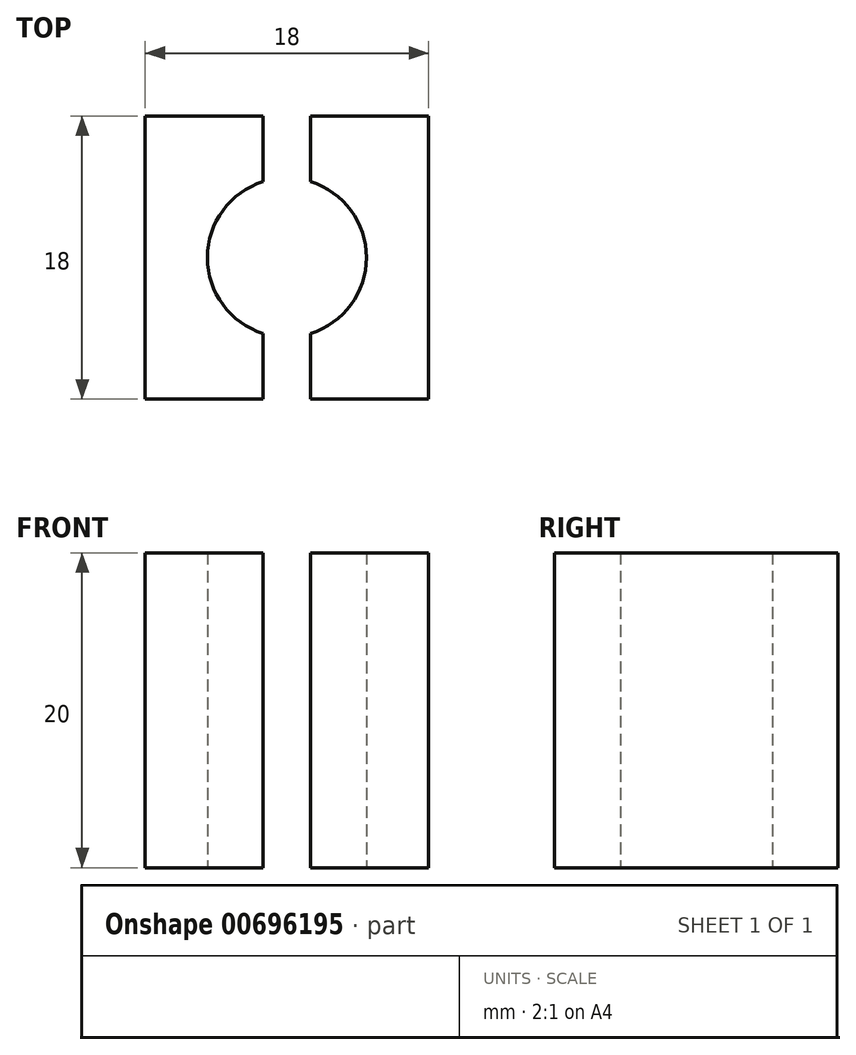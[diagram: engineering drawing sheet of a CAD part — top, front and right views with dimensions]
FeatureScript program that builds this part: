
annotation { "Feature Type Name" : "Feature", "Feature Type Description" : "" }
export const myFeature = defineFeature(function(context is Context, id is Id, definition is map)
    precondition{}
    {
        {
            var Q0;
            Q0=qCreatedBy(makeId("Top.planeOp"),FACE);
            var sketch = newSketch(context, id + "F0", { "sketchPlane" : qUnion([Q0])});
            skArc(sketch, "E0", {"start": v(1.5, -4.82) * mm, "mid": v(5.05, 0) * mm, "end": v(1.5, 4.82) * mm});
            skLineSegment(sketch, "E1.bottom", {"start": v(9, 9) * mm, "end": v(1.5, 9) * mm});
            skLineSegment(sketch, "E1.top", {"start": v(9, -9) * mm, "end": v(1.5, -9) * mm});
            skLineSegment(sketch, "E1.left", {"start": v(9, 9) * mm, "end": v(9, -9) * mm});
            skLineSegment(sketch, "E1.right", {"start": v(-9, 9) * mm, "end": v(-9, -9) * mm});
            skLineSegment(sketch, "E2.left", {"start": v(-1.5, 9) * mm, "end": v(-1.5, 4.82) * mm});
            skLineSegment(sketch, "E2.right", {"start": v(1.5, 9) * mm, "end": v(1.5, 4.82) * mm});
            skLineSegment(sketch, "E3.trimOffspring", {"start": v(-1.5, 9) * mm, "end": v(-9, 9) * mm});
            skLineSegment(sketch, "E4.trimOffspring", {"start": v(-1.5, -9) * mm, "end": v(-9, -9) * mm});
            skArc(sketch, "E5.trimOffspring", {"start": v(-1.5, 4.82) * mm, "mid": v(-5.05, 0) * mm, "end": v(-1.5, -4.82) * mm});
            skLineSegment(sketch, "E6.trimOffspring", {"start": v(-1.5, -4.82) * mm, "end": v(-1.5, -9) * mm});
            skLineSegment(sketch, "E7.trimOffspring", {"start": v(1.5, -4.82) * mm, "end": v(1.5, -9) * mm});
            skSolve(sketch);
        }
        {
            var Q0;
            Q0 = qSketchRegion(id + "F0", true);
            extrude(context, id + "F1", {"entities" : qUnion([Q0]), "depth" : 20 * mm, "offsetDistance" : 25 * mm});
        }
    });
